# Revit family: 5LDS5436B75B.V2,B2B.V2,B75T,B2T
name_source: partatom
category: Plumbing Fixtures
revit_build: Autodesk Revit LT 2017 (Build: 20160225_1515(x64)
units: mm (PartAtom-declared; Revit-internal decimal feet)

## family parameters
Always vertical = Yes
Cut with Voids When Loaded = No
OmniClass Number = 23.45.05.14.17
OmniClass Title = Showers
Part Type = Normal
Room Calculation Point = No
Round Connector Dimension = Use Diameter
Shared = No
Work Plane-Based = No

## types (4) — shared parameters
Assembly Code = D2010710
Keynote = 22 40 00.B3
Manufacturer = Best Bath Systems, Inc.
Type Comments = Barrier Free
URL = http://www.bestbath.com
Unit Depth = 37"
Unit Width = 54"

## per-type parameters (varying)
| type | Description | Model | Threshold Height | Unit Height |
| 5LDS5436B75B.V2 | Diamond Tile, Traditional Bull Nose Threshold | 5LDS5436B75B | 3/4" | 81" |
| 5LDS5436B2B.V2 | Diamond Tile, Beveled Threshold | 5LDS5436B2B | 2" | 82 1/4" |
| 5LDS5436B75T | Diamond Tile, Traditional Bull Nose Threshold | 5LDS5436B75T | 3/4" | 81" |
| 5LDS5436B2T | Traditional Bull Nose Threshold | 5LDS5436B2T | 2" | 82 1/4" |

## geometry (parser evidence)
native form markers: Sweep x2
no freeform markers — native parametric forms only
